# Revit family: Hager-VOLTA-Flush_mounted-IP30-With_Cover-With_DIN-Hosted-AT-de
name_source: partatom
category: Electrical Equipment
units: mm (PartAtom-declared; Revit-internal decimal feet)

## family parameters
Cut with Voids When Loaded = No
Host = Face
Maintain Annotation Orientation = Yes
Panel Configuration = Two Columns, Circuits Across
Part Type = Panelboard
Room Calculation Point = No
Round Connector Dimension = Use Diameter
Shared = No

## types (15) — shared parameters
BC_MODEL_ID = 1547047
BC_OBJECT_ID = 513454
BC_OBJECT_VERSION = #3
Code hager = ADD-EC000214_EU
EF000003 - Montageart = Unterputz
EF000008 - Breite = 348 mm  [stored 1.14173 ft]
EF000024 - UV-beständig = No
EF000049 - Tiefe = 98 mm  [stored 0.321522 ft]
EF000116 - RAL-Nummer = 9010
EF000218 - Einbautiefe = 89 mm  [stored 0.291995 ft]
EF000846 - Einbaubreite = 315 mm
EF001062 - EMV-Ausführung = No
EF001134 - DIN-Schiene = Yes
EF002950 - Breite in Teilungseinheiten = 12
EF005474 - Schutzart (IP) = IP30
EF006244 - Transparenter Deckel/Tür = No
EF006306 - Mit Schloss = No
ETIM class code = EC000214
ETIM class name = Small distribution board
HG000002-Mit tür = Yes
HG000003-Bereich = VOLTA
HG000005-Dicke = 2 mm  [stored 0.00656168 ft]
HG000006-Unterputz = Yes
HG000009-Doppelflügeligen Tür = No
HG000010-Asymmetrische Türen = No
HG000012-Türschwenkwinkel = 90.00°
HG000013-Tür links = No
HG000014-Tür rechts = Yes
HG000015-Sichtbarkeit der Türöffnung = Yes
HG000016-3D-Türsichtbarkeit = Yes
HG000017-Distanz zwischen den Polen = 18 mm  [stored 0.0590551 ft]
HG000060-RAL-number = 9010
HG000099-Onfly Template ID-de-AT = 507532
HGEF0002950-Breite in Teilungseinheiten = 12
Manufacturer = Hager
Name = VOLTA-Flush_mounted-IP30-With_Cover-With_DIN-AT
Name BIM&CO = Electricity
Name hager = ADD_Enclosures_EC000214
Uniformat = Low Tension Service & Dist.
Uniformat code = D501001
zero-valued in all types: Default Elevation, EF001131 - Innentiefe, HG000007-Anzahl der leeren Spalten

## per-type parameters (varying)
| type | BC_VARIANT_ID | EF000007 - Farbe | EF000040 - Höhe | EF000118 - Mit Montageplatte | EF000266 - Anzahl der Reihen | EF000332 - Einbauhöhe | EF001088 - Anbaumöglichkeit | EF004462 - Art der Schließung | EF009212 - Ausführung Deckel | EF015776 - Erdungsklemmenblock | EF015777 - Neutralleiterklemmenblock | EF015941 - Signaldurchlassende Tür | HG000001-Anzahl der Spalten | HG000004-Herstellerreferenz | HG000008-Anzahl der leeren Reihen | HG000011-Leere Reihen von unten | HGEF000266-Anzahl der Reihen |
| VOLTA-Flush_mounted_W348_H356_D98_12_Modular_Spacing-VU12AT | 1174021 | weiß | 356 mm  [stored 1.16798 ft] | No | 1 | 321 mm  [stored 1.05315 ft] | Yes | sonstige | mit Ausschnitt | Yes | Yes | No | 1 | VU12AT | 0 | No | 1 |
| VOLTA-Flush_mounted_W348_H505_D98_12_Modular_Spacing-VU24AT | 1174022 | weiß | 505 mm  [stored 1.65682 ft] | No | 2 | 470 mm  [stored 1.54199 ft] | Yes | sonstige | mit Ausschnitt | Yes | Yes | No | 1 | VU24AT | 0 | No | 2 |
| VOLTA-Flush_mounted_W348_H505_D98_12_Modular_Spacing-VU24NWB | 1174023 | weiß | 505 mm  [stored 1.65682 ft] | Yes | 0 | 470 mm  [stored 1.54199 ft] | Yes | sonstige | mit Ausschnitt | No | No | No | 0 | VU24NWB | 0 | No | 0 |
| VOLTA-Flush_mounted_W348_H630_D98_12_Modular_Spacing-VU36AT | 1174024 | weiß | 630 mm  [stored 2.06693 ft] | No | 3 | 595 mm  [stored 1.9521 ft] | Yes | sonstige | mit Ausschnitt | Yes | Yes | No | 1 | VU36AT | 0 | No | 3 |
| VOLTA-Flush_mounted_W348_H630_D98_12_Modular_Spacing-VU36CJG | 1174025 | weiß | 630 mm  [stored 2.06693 ft] | No | 3 | 595 mm  [stored 1.9521 ft] | Yes | sonstige | mit Ausschnitt | Yes | No | No | 1 | VU36CJG | 0 | No | 3 |
| VOLTA-Flush_mounted_W348_H630_D98_12_Modular_Spacing-VU36NWB | 1174026 | weiß | 630 mm  [stored 2.06693 ft] | Yes | 0 | 595 mm  [stored 1.9521 ft] | Yes | sonstige | mit Ausschnitt | No | No | No | 0 | VU36NWB | 0 | No | 0 |
| VOLTA-Flush_mounted_W348_H630_D98_12_Modular_Spacing-VU36WWH | 1174027 | weiß | 630 mm  [stored 2.06693 ft] | Yes | 0 | 595 mm  [stored 1.9521 ft] | Yes | sonstige | mit Ausschnitt | No | No | Yes | 0 | VU36WWH | 0 | No | 0 |
| VOLTA-Flush_mounted_W348_H755_D98_12_Modular_Spacing-VU48AT | 1174028 | weiß | 755 mm  [stored 2.47703 ft] | No | 4 | 720 mm  [stored 2.3622 ft] | Yes | sonstige | mit Ausschnitt | Yes | Yes | No | 1 | VU48AT | 0 | No | 4 |
| VOLTA-Flush_mounted_W348_H755_D98_12_Modular_Spacing-VU48NWB | 1174029 | weiß | 755 mm  [stored 2.47703 ft] | Yes | 0 | 720 mm  [stored 2.3622 ft] | Yes | sonstige | mit Ausschnitt | No | No | No | 0 | VU48NWB | 0 | No | 0 |
| VOLTA-Flush_mounted_W348_H880_D98_12_Modular_Spacing-VU602NWH | 1174031 |  | 880 mm  [stored 2.88714 ft] | No | 6 | 865 mm  [stored 2.83793 ft] | No |  |  | No | No | No | 1 | VU602NWH | 4 | Yes | 6 |
| VOLTA-Flush_mounted_W348_H880_D98_12_Modular_Spacing-VU602WWH | 1174032 |  | 880 mm  [stored 2.88714 ft] | No | 6 | 865 mm  [stored 2.83793 ft] | No |  |  | No | No | No | 1 | VU602WWH | 4 | Yes | 6 |
| VOLTA-Flush_mounted_W348_H880_D98_12_Modular_Spacing-VU603NWH | 1174034 |  | 880 mm  [stored 2.88714 ft] | No | 6 | 865 mm  [stored 2.83793 ft] | No |  |  | No | No | No | 1 | VU603NWH | 3 | Yes | 6 |
| VOLTA-Flush_mounted_W348_H880_D98_12_Modular_Spacing-VU603WWH | 1174036 |  | 880 mm  [stored 2.88714 ft] | No | 6 | 865 mm  [stored 2.83793 ft] | No |  |  | No | No | No | 1 | VU603WWH | 3 | Yes | 6 |
| VOLTA-Flush_mounted_W348_H880_D98_12_Modular_Spacing-VU60AT | 1174038 | weiß | 880 mm  [stored 2.88714 ft] | No | 5 | 845 mm  [stored 2.77231 ft] | Yes | sonstige | mit Ausschnitt | Yes | Yes | No | 1 | VU60AT | 0 | No | 5 |
| VOLTA-Flush_mounted_W348_H880_D98_12_Modular_Spacing-VU60NWB | 1174040 | weiß | 880 mm  [stored 2.88714 ft] | Yes | 0 | 865 mm  [stored 2.83793 ft] | Yes | sonstige | mit Ausschnitt | No | No | No | 0 | VU60NWB | 0 | No | 0 |

note: column(s) folded — value = type name in every type: Reference

note: [stored X ft] marks values corroborated as IEEE doubles in the binary element streams (Revit-internal decimal feet)

## geometry (parser evidence)
native form markers: Sweep x13
no freeform markers — native parametric forms only
